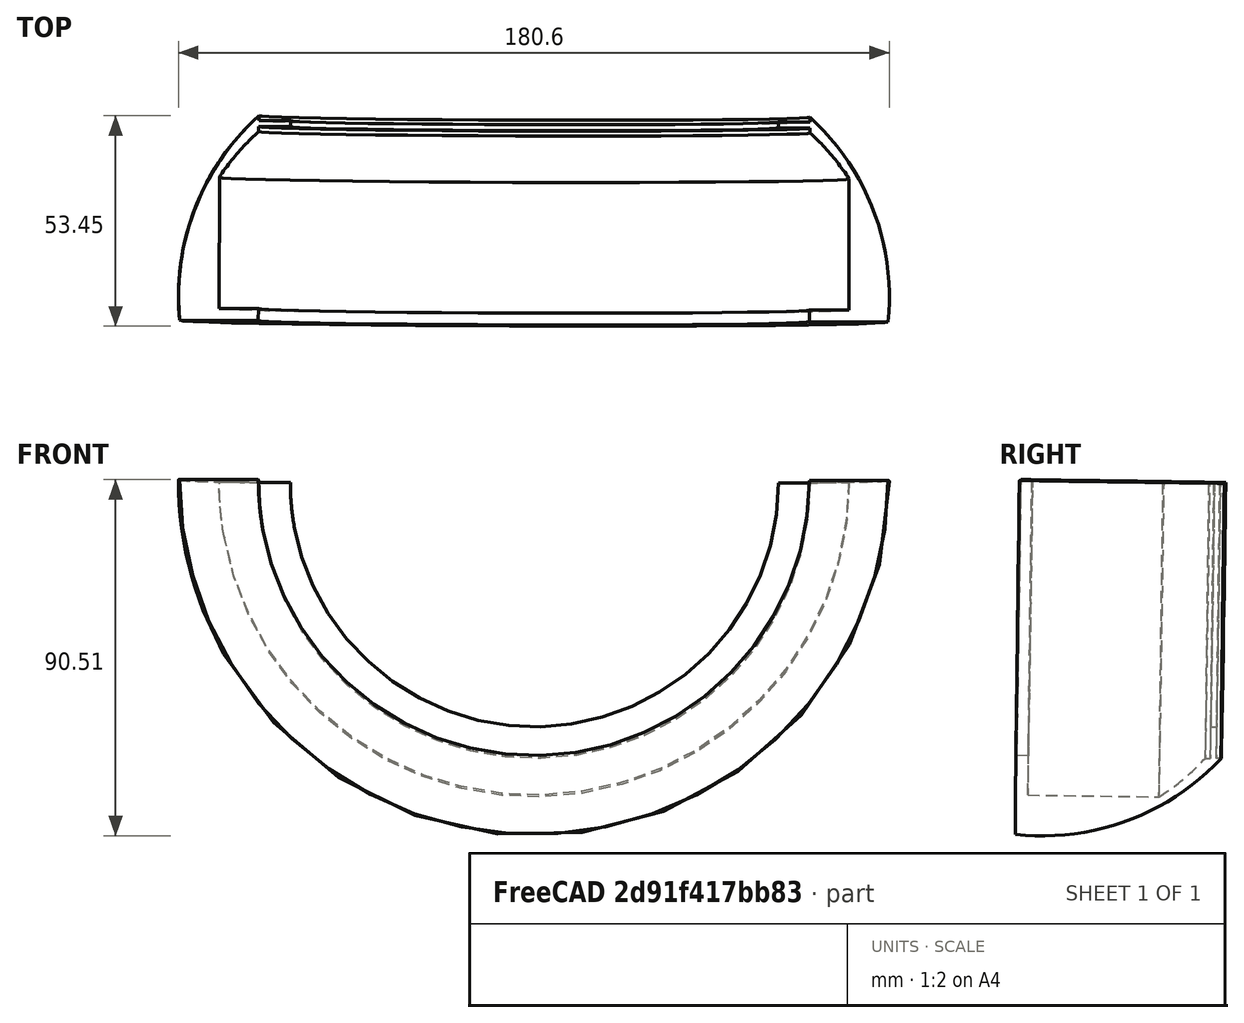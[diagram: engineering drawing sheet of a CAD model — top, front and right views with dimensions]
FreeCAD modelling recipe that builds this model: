
FCSTD DOCUMENT
Label: base
objects: Part::Feature×2, Sketcher::SketchObject×1, Part::Revolution×1
note: 4 computed .brp shape members not serialized (recipe doc carries the construction recipe); baked Part::Feature solids carry a one-line shape summary decoded from their .brp

FEATURE [Sketcher::SketchObject] Sketch
  sketch-geometry (13):
    g0: LineSegment StartX=70 StartY=0 StartZ=0 EndX=90 EndY=0 EndZ=0
    g1: LineSegment StartX=70 StartY=3 StartZ=0 EndX=80 EndY=3 EndZ=0
    g2: LineSegment StartX=80 StartY=3 StartZ=0 EndX=80 EndY=36.3415 EndZ=0
    g3: LineSegment StartX=70 StartY=3 StartZ=0 EndX=70 EndY=0 EndZ=0
    g4: GeomPoint [constr] X=70 Y=48 Z=0
    g5: ArcOfCircle CenterX=30.5981 CenterY=4.08542 CenterZ=0 NormalX=0 NormalY=0 NormalZ=1 Radius=59 StartAngle=0.578433 EndAngle=0.839509
    g6: ArcOfCircle CenterX=28.3024 CenterY=6.11632 CenterZ=0 NormalX=0 NormalY=0 NormalZ=1 Radius=62 StartAngle=6.18437 EndAngle=7.11634
    g7: GeomPoint [constr] X=80 Y=40.3415 Z=0
    g8: LineSegment StartX=70 StartY=48 StartZ=0 EndX=70 EndY=49.25 EndZ=0
    g9: LineSegment StartX=70 StartY=49.25 StartZ=0 EndX=65 EndY=49.25 EndZ=0
    g10: LineSegment StartX=70 StartY=52 StartZ=0 EndX=70 EndY=50.75 EndZ=0
    g11: LineSegment StartX=70 StartY=50.75 StartZ=0 EndX=65 EndY=50.75 EndZ=0
    g12: LineSegment StartX=65 StartY=49.25 StartZ=0 EndX=65 EndY=50.75 EndZ=0
  constraints (38):
    c: PointOnObject(g0,g-1)
    c: Horizontal(g0)
    c: Distance(g0) = 20
    c: Horizontal(g1)
    c: Distance(g1) = 10
    c: Coincident(g2,g1)
    c: Vertical(g2)
    c: DistanceY(g1,g0) = -3
    c: Distance(g-1,g0) = 70
    c: Coincident(g3,g1)
    c: Coincident(g3,g0)
    c: Perpendicular(g3,g0)
    c: Coincident(g5,g4)
    c: Coincident(g5,g2)
    c: Coincident(g6,g0)
    c: DistanceY(g6,g0) = -52
    c: PointOnObject(g7,g6)
    c: DistanceX(g7,g2) = 0
    c: DistanceX(g4,g6) = 0
    c: DistanceY(g4,g6) = 4
    c: DistanceX(g4,g1) = 0
    c: DistanceY(g2,g7) = 4
    c: Radius(g6) = 62
    c: Radius(g5) = 59
    c: Coincident(g8,g4)
    c: Vertical(g8)
    c: Coincident(g9,g8)
    c: Horizontal(g9)
    c: Coincident(g10,g6)
    c: Coincident(g11,g10)
    c: Horizontal(g11)
    c: Coincident(g12,g9)
    c: Coincident(g12,g11)
    c: Vertical(g12)
    c: Distance(g8) = 1.25
    c: Distance(g12) = 1.5
    c: Distance(g11) = 5
    c: Perpendicular(g10,g11)
FEATURE [Part::Revolution] Revolve
  Angle = 180
  Axis = (0,1,0)
  Base = (0,0,0)
  Placement = pos=(83.3546,-60.7808,30.1124) rot=(-0.978841,0.100932,-0.177995;0.014335rad)
  Source = -> Sketch
FEATURE [Part::Feature] Face
  shape: bbox 28.19 x 52.05 x 0.7297 mm, 1 faces, 0 solids (baked)
FEATURE [Part::Feature] Face001
  shape: bbox 28.42 x 51.99 x 0.7583 mm, 1 faces, 0 solids (baked)
